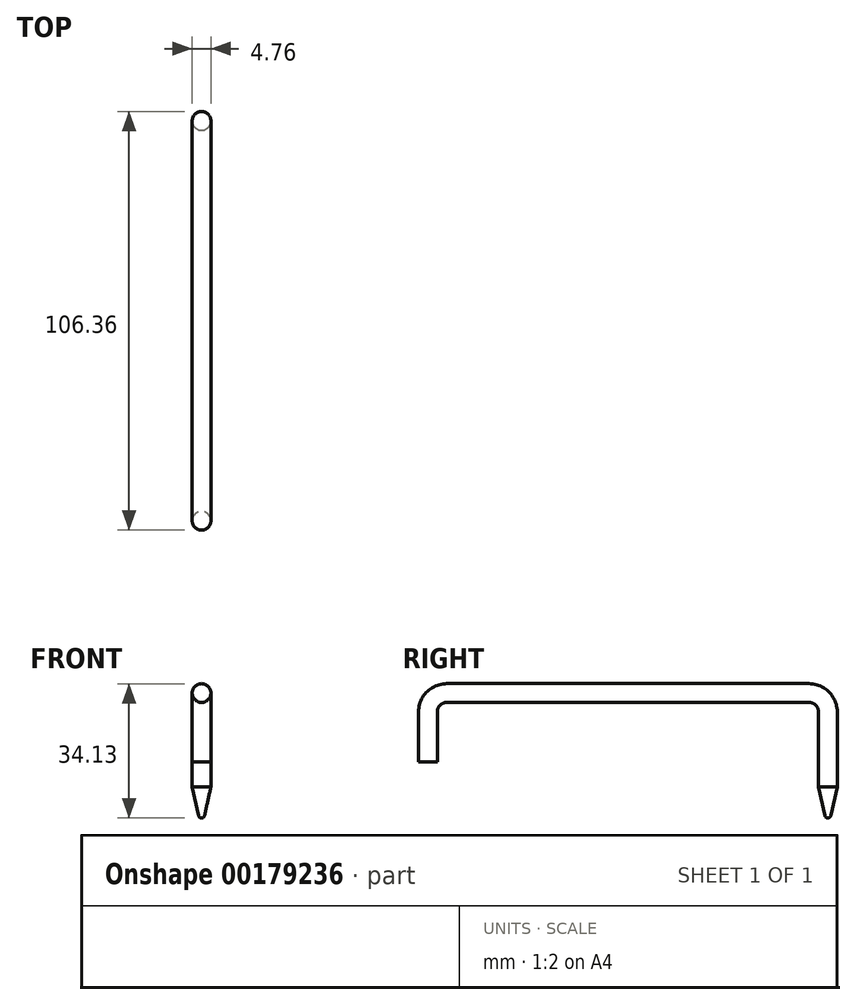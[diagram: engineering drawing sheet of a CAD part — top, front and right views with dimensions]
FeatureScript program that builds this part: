
annotation { "Feature Type Name" : "Feature", "Feature Type Description" : "" }
export const myFeature = defineFeature(function(context is Context, id is Id, definition is map)
    precondition{}
    {
        {
            var Q0;
            Q0=qCreatedBy(makeId("Right.planeOp"),FACE);
            var sketch = newSketch(context, id + "F0", { "sketchPlane" : qUnion([Q0])});
            skLineSegment(sketch, "E0", {"start": v(0, 0) * mm, "end": v(0, 12.7) * mm});
            skArc(sketch, "E1", {"start": v(0, 12.7) * mm, "mid": v(1.4, 16.07) * mm, "end": v(4.76, 17.46) * mm});
            skLineSegment(sketch, "E2", {"start": v(4.76, 17.46) * mm, "end": v(96.84, 17.46) * mm});
            skArc(sketch, "E3", {"start": v(96.84, 17.46) * mm, "mid": v(100.2, 16.07) * mm, "end": v(101.6, 12.7) * mm});
            skLineSegment(sketch, "E4", {"start": v(101.6, -6.35) * mm, "end": v(101.6, -13.5) * mm});
            skLineSegment(sketch, "E5", {"start": v(101.6, -6.35) * mm, "end": v(103.98, -6.35) * mm});
            skLineSegment(sketch, "E6", {"start": v(103.98, -6.35) * mm, "end": v(102.36, -13.68) * mm});
            skArc(sketch, "E7", {"start": v(102.36, -13.68) * mm, "mid": v(102.09, -14.12) * mm, "end": v(101.6, -14.29) * mm});
            skLineSegment(sketch, "E8", {"start": v(101.6, -14.29) * mm, "end": v(101.6, -13.5) * mm});
            skLineSegment(sketch, "E9", {"start": v(101.6, 12.7) * mm, "end": v(101.6, -6.35) * mm});
            skSolve(sketch);
        }
        {
            var Q0;
            Q0=qCreatedBy(makeId("Top.planeOp"),FACE);
            var sketch = newSketch(context, id + "F1", { "sketchPlane" : qUnion([Q0])});
            skCircle(sketch, "E10", {"center": v(0, 0) * mm, "radius": 2.38 * mm});
            skSolve(sketch);
        }
        {
            var Q0;
            Q0=makeQuery(id+"F1.imprint","IMPRINT",FACE,{"disambiguationData":[TD([[makeQuery(id+"F1.imprint","IMPRINT",EDGE,{"derivedFrom":sQuery(id+"F1.wireOp",EDGE,"E10")}),1.0]])]});
            var Q1;
            Q1=sQuery(id+"F1.wireOp",EDGE,"E10");
            var Q2;
            Q2=sQuery(id+"F0.wireOp",EDGE,"E0");
            var Q3;
            Q3=sQuery(id+"F0.wireOp",EDGE,"E1");
            var Q4;
            Q4=sQuery(id+"F0.wireOp",EDGE,"E2");
            var Q5;
            Q5=sQuery(id+"F0.wireOp",EDGE,"E3");
            var Q6;
            Q6=sQuery(id+"F0.wireOp",EDGE,"E9");
            sweep(context, id + "F2", {"profiles" : qUnion([Q0]), "surfaceProfiles" : qUnion([Q1]), "path" : qUnion([Q2, Q3, Q4, Q5, Q6])});
        }
        {
            var Q0;
            Q0=makeQuery(id+"F0.imprint","IMPRINT",FACE,{"disambiguationData":[TD([[makeQuery(id+"F0.imprint","IMPRINT",EDGE,{"derivedFrom":sQuery(id+"F0.wireOp",EDGE,"E4")}),1.0]])]});
            var Q1;
            Q1=sQuery(id+"F0.wireOp",EDGE,"E4");
            revolve(context, id + "F3", {"operationType" : NewBodyOperationType.ADD, "entities" : qUnion([Q0]), "axis" : qUnion([Q1]), "revolveType" : RevolveType.FULL});
        }
    });
